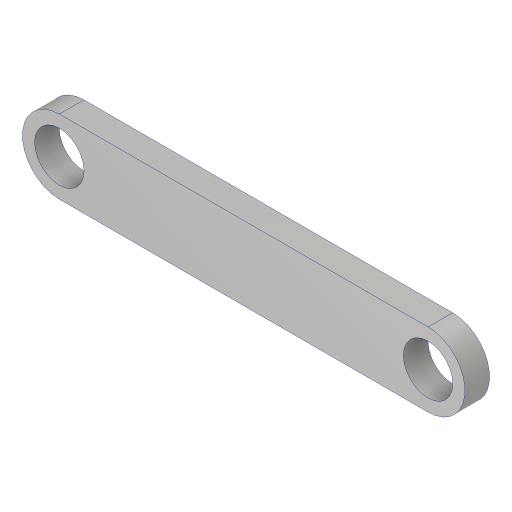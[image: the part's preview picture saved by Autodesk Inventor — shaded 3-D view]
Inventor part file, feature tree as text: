
AUTODESK INVENTOR PART (.ipt)
format: ipt  version: 2023.2 (Build 272271000, 271)  size: 140,288 bytes
history: native  units: mm
features: extrude x3, sketch x3, fillet x2, other x1, projected_geometry x1
ambient origin geometry x8: Origin, YZ Plane, XZ Plane, XY Plane, X Axis, Y Axis, Z Axis, Center Point
bodies: Body1 (feature_tree)
feature tree (10):
  other  "솔리드1"
  extrude  "돌출1"  Depth=36.0mm
  fillet  "모깎기1"  [1 undecoded]
  fillet  "모깎기2"  Radius=6.0mm
  extrude  "돌출4"  TaperAngle=90.0deg  [1 undecoded]
  extrude  "돌출5"  Depth=6.0mm
  sketch  "스케치1"
  sketch  "스케치4"
  sketch  "스케치5"
  projected_geometry  "투영된 루프2"
note: 2 required parameter values undecoded (feature->parameter linkage not recoverable at this tier; creation-order binding heuristic only, values carry confidence <= 0.55)
